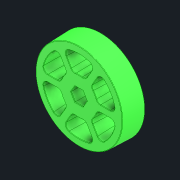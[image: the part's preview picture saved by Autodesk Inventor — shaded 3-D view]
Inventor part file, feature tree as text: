
AUTODESK INVENTOR PART (.ipt)
format: ipt  version: 2021 (Build 250183000, 183)  size: 704,512 bytes
history: native  units: in
note: dims shown in document units (in); Inventor stores cm internally (conversion verified against a paired STEP export)
features: fillet x1
ambient origin geometry x8: Origin, YZ Plane, XZ Plane, XY Plane, X Axis, Y Axis, Z Axis, Center Point
bodies: Solid1 (feature_tree)
feature tree (1):
  fillet  "Fillet3"  [1 undecoded]
note: 1 required parameter value undecoded (feature->parameter linkage not recoverable at this tier; creation-order binding heuristic only, values carry confidence <= 0.55)
